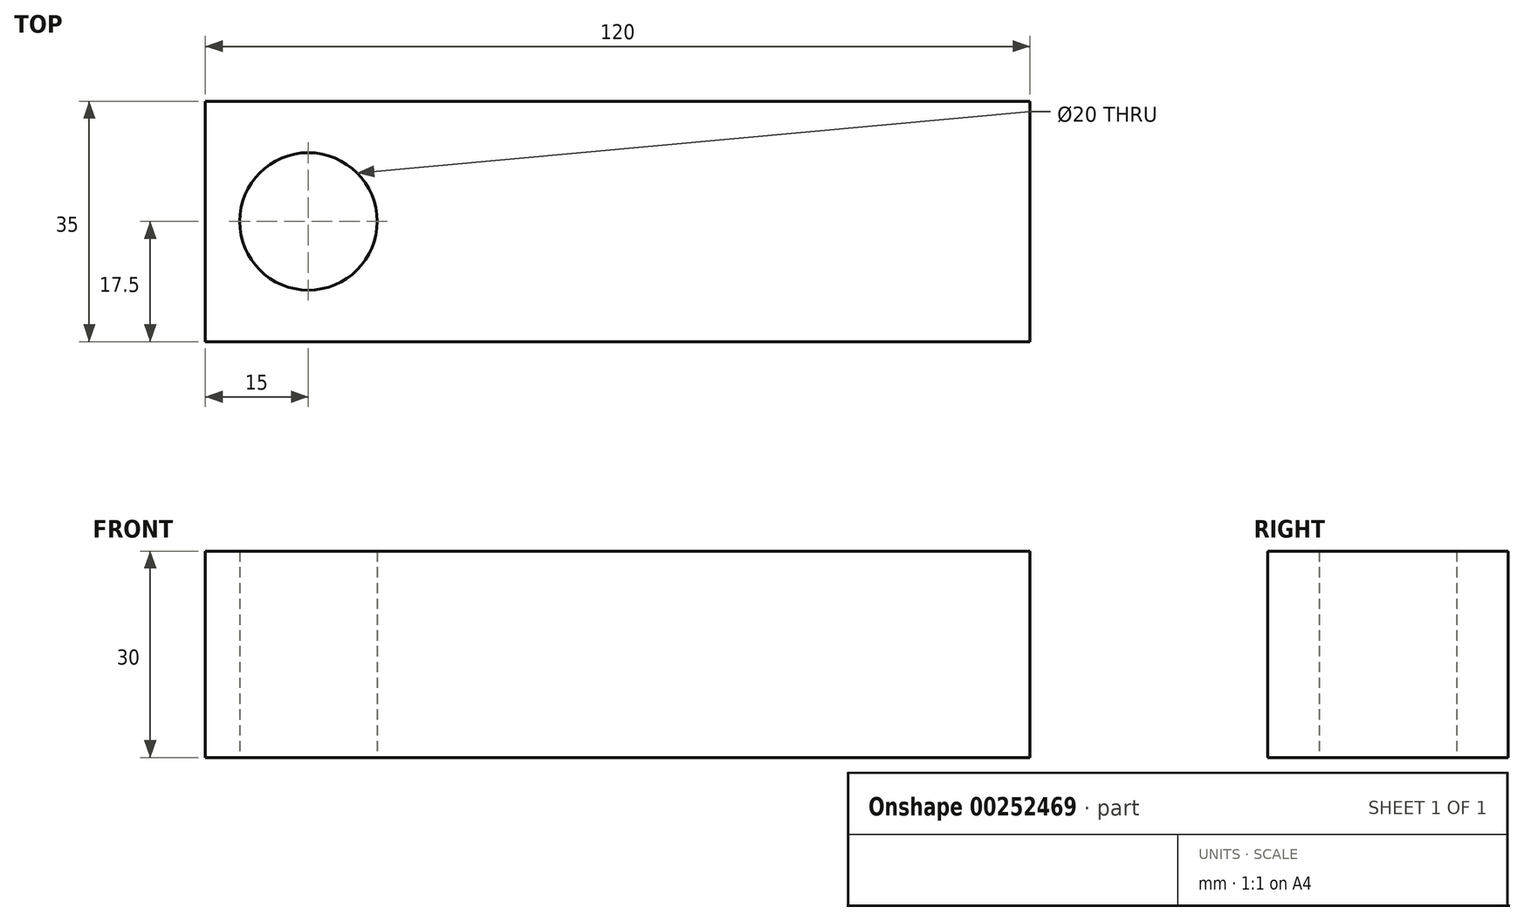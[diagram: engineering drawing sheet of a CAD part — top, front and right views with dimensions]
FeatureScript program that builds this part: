
annotation { "Feature Type Name" : "Feature", "Feature Type Description" : "" }
export const myFeature = defineFeature(function(context is Context, id is Id, definition is map)
    precondition{}
    {
        {
            var Q0;
            Q0=qCreatedBy(makeId("Top.planeOp"),FACE);
            var sketch = newSketch(context, id + "F0", { "sketchPlane" : qUnion([Q0])});
            skLineSegment(sketch, "E0.bottom", {"start": v(-60, 17.5) * mm, "end": v(60, 17.5) * mm});
            skLineSegment(sketch, "E0.top", {"start": v(-60, -17.5) * mm, "end": v(60, -17.5) * mm});
            skLineSegment(sketch, "E0.left", {"start": v(-60, 17.5) * mm, "end": v(-60, -17.5) * mm});
            skLineSegment(sketch, "E0.right", {"start": v(60, 17.5) * mm, "end": v(60, -17.5) * mm});
            skPoint(sketch, "E0.middle", {"position": v(0, 0) * mm});
            skCircle(sketch, "E1", {"center": v(-45, 0) * mm, "radius": 10 * mm});
            skSolve(sketch);
        }
        {
            var Q0;
            Q0=makeQuery(id+"F0.imprint","IMPRINT",FACE,{"disambiguationData":[TD([[makeQuery(id+"F0.imprint","IMPRINT",EDGE,{"derivedFrom":sQuery(id+"F0.wireOp",EDGE,"E0.bottom")}),-1.0]])]});
            extrude(context, id + "F1", {"entities" : qUnion([Q0]), "depth" : 5 * mm});
        }
        {
            var Q0;
            Q0=makeQuery(id+"F1.opExtrude","CAP_FACE",FACE,{"disambiguationData":[OSD([sQuery(id+"F0.wireOp",EDGE,"E0.bottom"),sQuery(id+"F0.wireOp",EDGE,"E0.top"),sQuery(id+"F0.wireOp",EDGE,"E0.left"),sQuery(id+"F0.wireOp",EDGE,"E0.right"),sQuery(id+"F0.wireOp",EDGE,"E1")])],"isStart":false});
            extrude(context, id + "F2", {"entities" : qUnion([Q0]), "operationType" : NewBodyOperationType.ADD, "depth" : 25 * mm});
        }
    });
